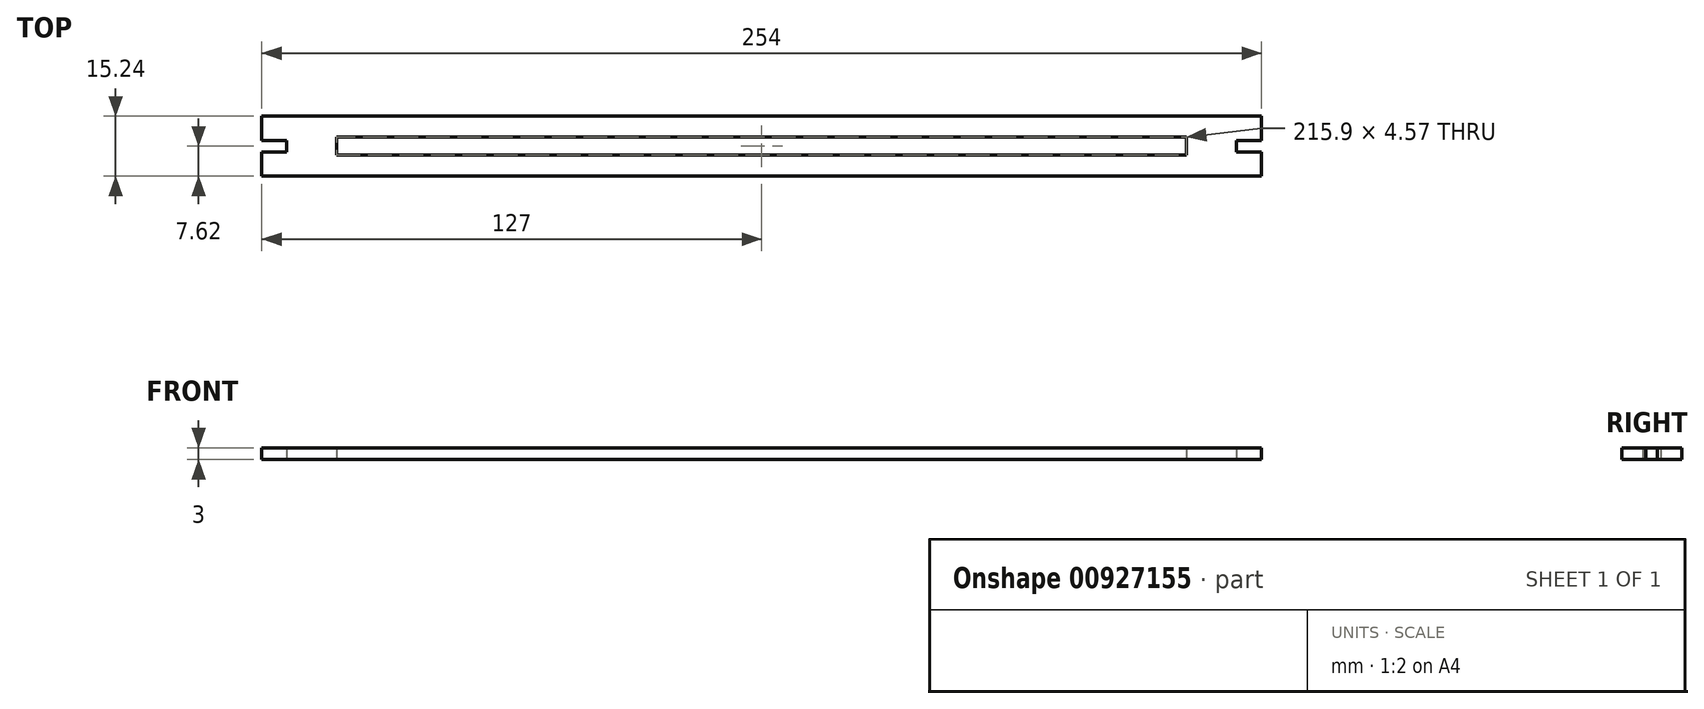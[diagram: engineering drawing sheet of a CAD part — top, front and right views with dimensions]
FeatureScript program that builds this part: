
annotation { "Feature Type Name" : "Feature", "Feature Type Description" : "" }
export const myFeature = defineFeature(function(context is Context, id is Id, definition is map)
    precondition{}
    {
        {
            var Q0;
            Q0=qCreatedBy(makeId("Top.planeOp"),FACE);
            var sketch = newSketch(context, id + "F0", { "sketchPlane" : qUnion([Q0])});
            skLineSegment(sketch, "E0.bottom", {"start": v(0, 0) * mm, "end": v(254, 0) * mm});
            skLineSegment(sketch, "E0.top", {"start": v(0, 15.24) * mm, "end": v(254, 15.24) * mm});
            skLineSegment(sketch, "E0.left", {"start": v(0, 0) * mm, "end": v(0, 15.24) * mm});
            skLineSegment(sketch, "E0.right", {"start": v(254, 0) * mm, "end": v(254, 15.24) * mm});
            skLineSegment(sketch, "E1.bottom", {"start": v(0, 9.12) * mm, "end": v(6.35, 9.12) * mm});
            skLineSegment(sketch, "E1.top", {"start": v(0, 6.12) * mm, "end": v(6.35, 6.12) * mm});
            skLineSegment(sketch, "E1.left", {"start": v(0, 9.12) * mm, "end": v(0, 6.12) * mm});
            skLineSegment(sketch, "E1.right", {"start": v(6.35, 9.12) * mm, "end": v(6.35, 6.12) * mm});
            skLineSegment(sketch, "E2", {"start": v(6.35, 7.62) * mm, "end": v(0, 7.62) * mm, "construction": true});
            skLineSegment(sketch, "E3", {"start": v(127, 15.24) * mm, "end": v(127, 0) * mm, "construction": true});
            skLineSegment(sketch, "E4.MirrorCS", {"start": v(247.65, 7.62) * mm, "end": v(254, 7.62) * mm, "construction": true});
            skLineSegment(sketch, "E5.MirrorCS", {"start": v(254, 9.12) * mm, "end": v(254, 6.12) * mm});
            skLineSegment(sketch, "E6.MirrorCS", {"start": v(254, 6.12) * mm, "end": v(247.65, 6.12) * mm});
            skLineSegment(sketch, "E7.MirrorCS", {"start": v(254, 9.12) * mm, "end": v(247.65, 9.12) * mm});
            skLineSegment(sketch, "E8.MirrorCS", {"start": v(247.65, 9.12) * mm, "end": v(247.65, 6.12) * mm});
            skLineSegment(sketch, "E9.bottom", {"start": v(19.05, 5.33) * mm, "end": v(234.95, 5.33) * mm});
            skLineSegment(sketch, "E9.top", {"start": v(19.05, 9.9) * mm, "end": v(234.95, 9.9) * mm});
            skLineSegment(sketch, "E9.left", {"start": v(19.05, 5.33) * mm, "end": v(19.05, 9.9) * mm});
            skLineSegment(sketch, "E9.right", {"start": v(234.95, 5.33) * mm, "end": v(234.95, 9.9) * mm});
            skPoint(sketch, "E9.middle", {"position": v(127, 7.62) * mm});
            skSolve(sketch);
        }
        {
            var Q0;
            {var subQ6=sQuery(id+"F0.wireOp",EDGE,"E0.bottom");Q0=makeQuery(id+"F0.imprint","IMPRINT",FACE,{"disambiguationData":[TD([[makeQuery(id+"F0.imprint","IMPRINT",EDGE,{"derivedFrom":subQ6}),1.0]])]});}
            extrude(context, id + "F1", {"entities" : qUnion([Q0]), "depth" : 3 * mm, "offsetDistance" : 25.4 * mm});
        }
    });
